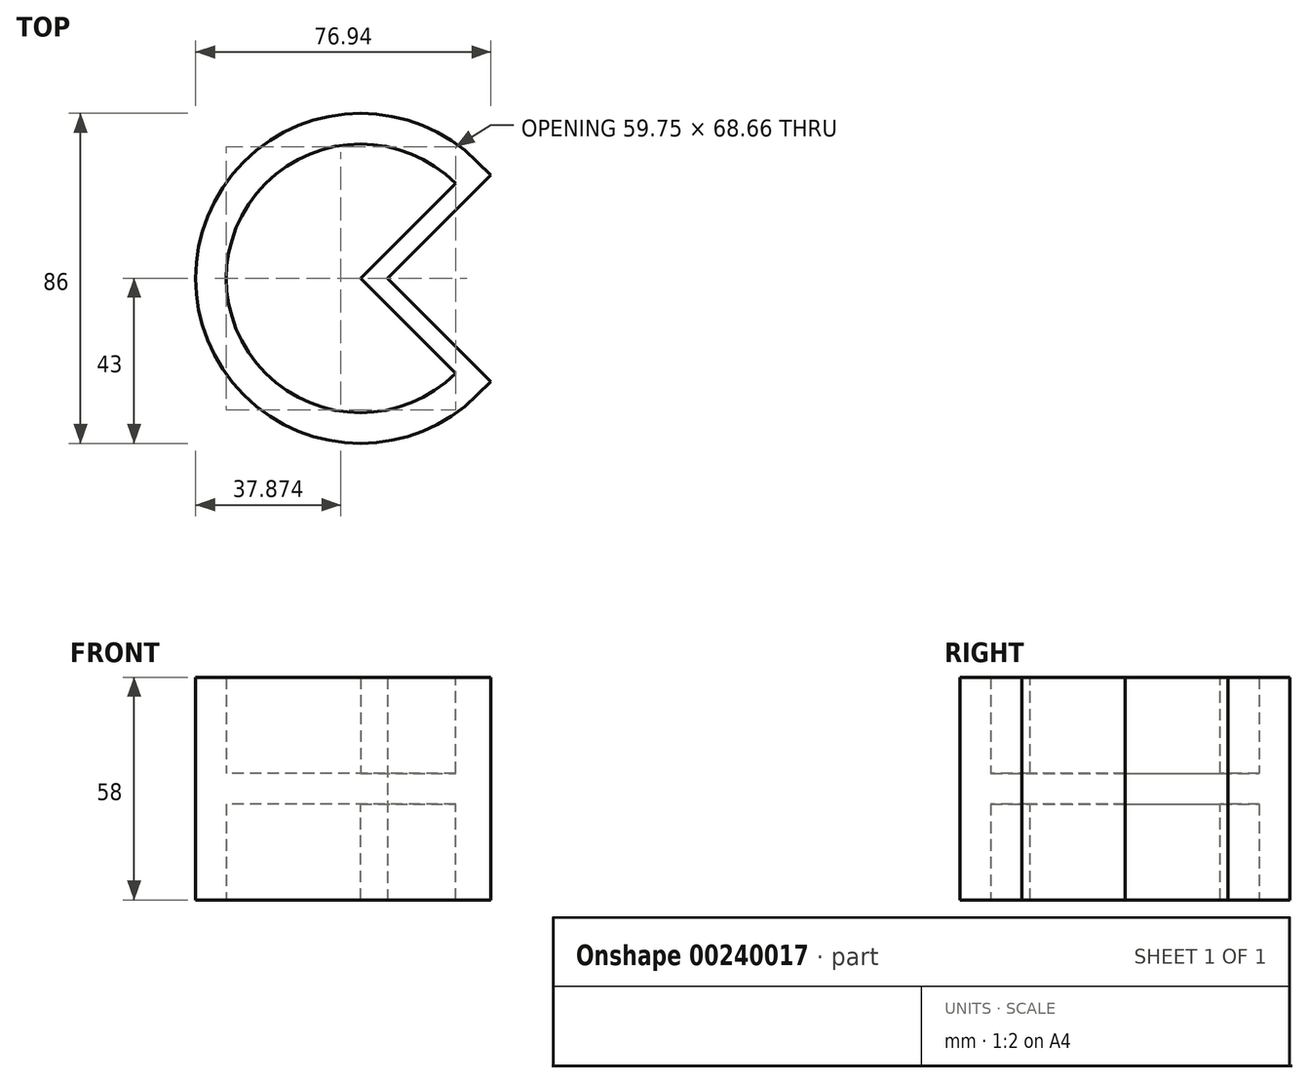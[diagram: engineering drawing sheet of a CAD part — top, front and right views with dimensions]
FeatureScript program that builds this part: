
annotation { "Feature Type Name" : "Feature", "Feature Type Description" : "" }
export const myFeature = defineFeature(function(context is Context, id is Id, definition is map)
    precondition{}
    {
        {
            var Q0;
            Q0=qCreatedBy(makeId("Front.planeOp"),FACE);
            var sketch = newSketch(context, id + "F0", { "sketchPlane" : qUnion([Q0])});
            skLineSegment(sketch, "E0.bottom", {"start": v(0, 4) * mm, "end": v(-35, 4) * mm});
            skLineSegment(sketch, "E0.top", {"start": v(0, -4) * mm, "end": v(-35, -4) * mm});
            skLineSegment(sketch, "E0.left", {"start": v(0, 4) * mm, "end": v(0, -4) * mm});
            skLineSegment(sketch, "E1.bottom", {"start": v(-35, -29) * mm, "end": v(-43, -29) * mm});
            skLineSegment(sketch, "E1.top", {"start": v(-35, 29) * mm, "end": v(-43, 29) * mm});
            skLineSegment(sketch, "E1.left", {"start": v(-35, -29) * mm, "end": v(-35, -4) * mm});
            skLineSegment(sketch, "E1.right", {"start": v(-43, -29) * mm, "end": v(-43, 29) * mm});
            skLineSegment(sketch, "E2.trimOffspring", {"start": v(-35, 4) * mm, "end": v(-35, 29) * mm});
            skLineSegment(sketch, "E3", {"start": v(0, -43.09) * mm, "end": v(0, 41.02) * mm, "construction": true});
            skSolve(sketch);
        }
        {
            var Q0;
            Q0=makeQuery(id+"F0.imprint","IMPRINT",FACE,{"disambiguationData":[TD([[makeQuery(id+"F0.imprint","IMPRINT",EDGE,{"derivedFrom":sQuery(id+"F0.wireOp",EDGE,"E0.bottom")}),1.0]])]});
            var Q1;
            Q1=sQuery(id+"F0.wireOp",EDGE,"E3");
            revolve(context, id + "F1", {"entities" : qUnion([Q0]), "axis" : qUnion([Q1]), "revolveType" : RevolveType.SYMMETRIC, "angle" : 270 * degree});
        }
        {
            var Q0;
            Q0=qCreatedBy(makeId("Top.planeOp"),FACE);
            var sketch = newSketch(context, id + "F2", { "sketchPlane" : qUnion([Q0])});
            skPoint(sketch, "E4.0", {"position": v(30.4, -30.4) * mm});
            skPoint(sketch, "E5.0", {"position": v(0, 0) * mm});
            skPoint(sketch, "E6.0", {"position": v(30.4, 30.4) * mm});
            skLineSegment(sketch, "E7", {"start": v(30.4, -30.4) * mm, "end": v(0, 0) * mm});
            skLineSegment(sketch, "E8", {"start": v(30.4, 30.4) * mm, "end": v(0, 0) * mm});
            skLineSegment(sketch, "E9", {"start": v(30.4, -30.4) * mm, "end": v(33.94, -26.87) * mm});
            skLineSegment(sketch, "E10", {"start": v(33.94, -26.87) * mm, "end": v(7.07, 0) * mm});
            skLineSegment(sketch, "E11", {"start": v(30.4, 30.4) * mm, "end": v(33.94, 26.87) * mm});
            skLineSegment(sketch, "E12", {"start": v(33.94, 26.87) * mm, "end": v(7.07, 0) * mm});
            skSolve(sketch);
        }
        {
            var Q0;
            Q0 = qSketchRegion(id + "F2", true);
            var Q1;
            Q1=makeQuery(id+"F1.opRevolve","SWEPT_FACE",FACE,{"disambiguationData":[OSD([sQuery(id+"F0.wireOp",EDGE,"E1.top")])]});
            extrude(context, id + "F3", {"entities" : qUnion([Q0]), "operationType" : NewBodyOperationType.ADD, "endBound" : BoundingType.UP_TO_SURFACE, "endBoundEntityFace" : qUnion([Q1]), "depth" : 25 * mm});
        }
        {
            var Q0;
            Q0=makeQuery(id+"F3.opExtrude","CAP_FACE",FACE,{"disambiguationData":[OSD([sQuery(id+"F2.wireOp",EDGE,"E7"),sQuery(id+"F2.wireOp",EDGE,"E8"),sQuery(id+"F2.wireOp",EDGE,"E9"),sQuery(id+"F2.wireOp",EDGE,"E10"),sQuery(id+"F2.wireOp",EDGE,"E11"),sQuery(id+"F2.wireOp",EDGE,"E12")])],"isStart":true});
            var Q1;
            Q1=makeQuery(id+"F1.opRevolve","SWEPT_FACE",FACE,{"disambiguationData":[OSD([sQuery(id+"F0.wireOp",EDGE,"E1.bottom")])]});
            extrude(context, id + "F4", {"entities" : qUnion([Q0]), "operationType" : NewBodyOperationType.ADD, "endBound" : BoundingType.UP_TO_SURFACE, "endBoundEntityFace" : qUnion([Q1]), "depth" : 25 * mm});
        }
    });
